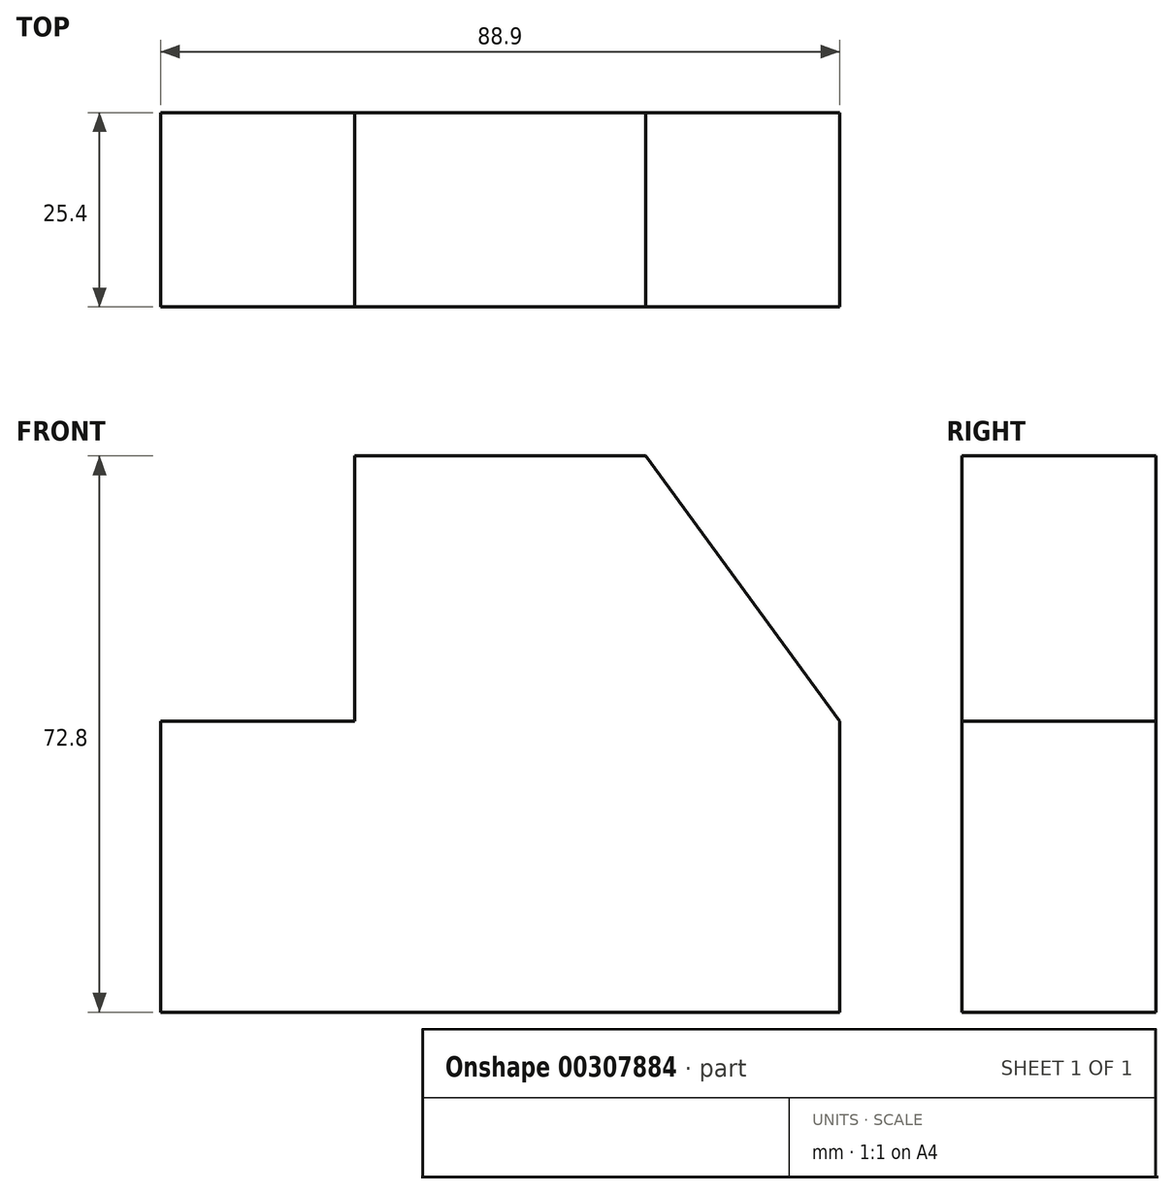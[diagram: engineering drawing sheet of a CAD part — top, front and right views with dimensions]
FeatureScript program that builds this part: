
annotation { "Feature Type Name" : "Feature", "Feature Type Description" : "" }
export const myFeature = defineFeature(function(context is Context, id is Id, definition is map)
    precondition{}
    {
        {
            var Q0;
            Q0=qCreatedBy(makeId("Front.planeOp"),FACE);
            var sketch = newSketch(context, id + "F0", { "sketchPlane" : qUnion([Q0])});
            skLineSegment(sketch, "E0", {"start": v(-60.26, -31.24) * mm, "end": v(28.64, -31.24) * mm});
            skLineSegment(sketch, "E1", {"start": v(28.64, -31.24) * mm, "end": v(28.64, 6.86) * mm});
            skLineSegment(sketch, "E2", {"start": v(-60.26, -31.24) * mm, "end": v(-60.26, 6.86) * mm});
            skLineSegment(sketch, "E3", {"start": v(-60.26, 6.86) * mm, "end": v(-34.86, 6.86) * mm});
            skLineSegment(sketch, "E4", {"start": v(-34.86, 6.86) * mm, "end": v(-34.86, 41.56) * mm});
            skLineSegment(sketch, "E5", {"start": v(-34.86, 41.56) * mm, "end": v(3.24, 41.56) * mm});
            skLineSegment(sketch, "E6", {"start": v(3.24, 41.56) * mm, "end": v(28.64, 6.86) * mm});
            skSolve(sketch);
        }
        {
            var Q0;
            Q0=makeQuery(id+"F0.imprint","IMPRINT",FACE,{"disambiguationData":[TD([[makeQuery(id+"F0.imprint","IMPRINT",EDGE,{"derivedFrom":sQuery(id+"F0.wireOp",EDGE,"E0")}),1.0]])]});
            extrude(context, id + "F1", {"entities" : qUnion([Q0]), "depth" : 25.4 * mm});
        }
    });
